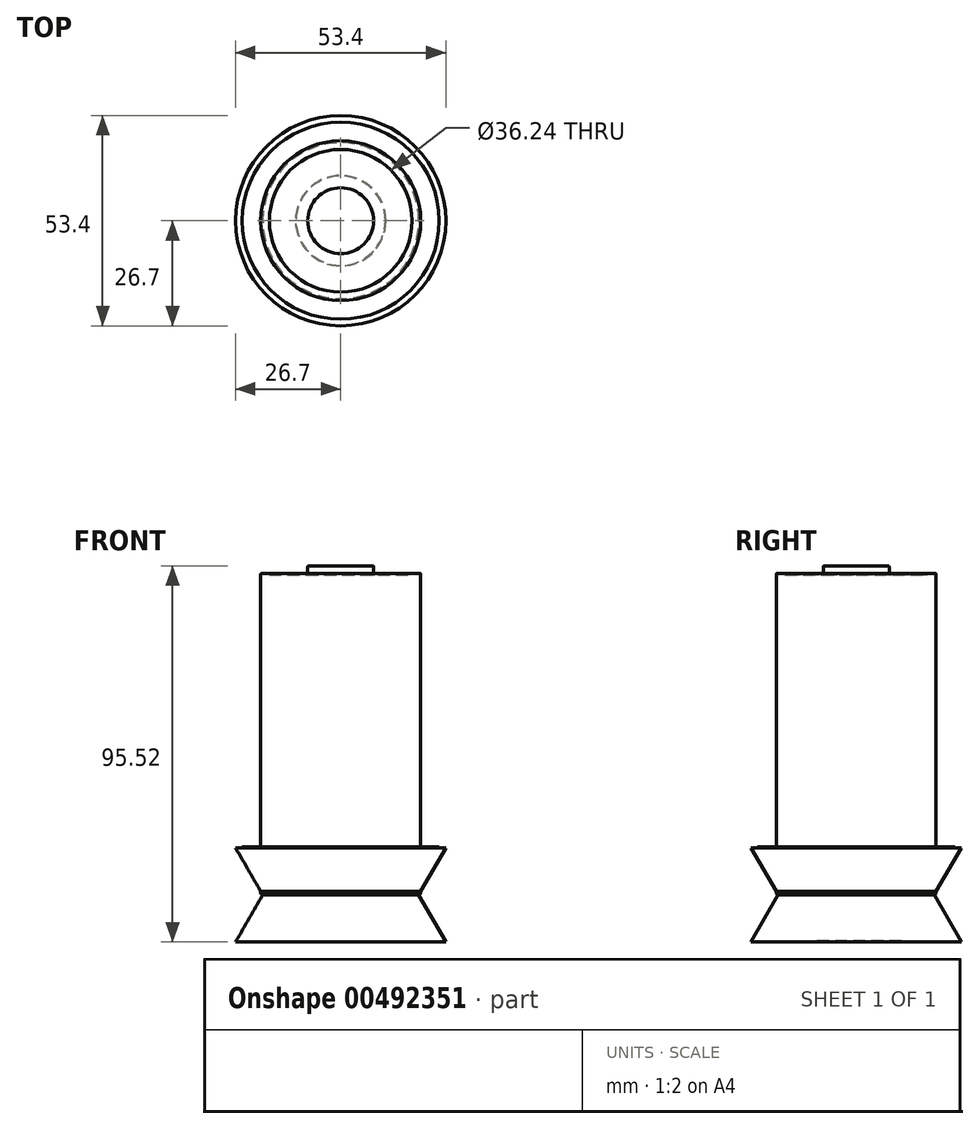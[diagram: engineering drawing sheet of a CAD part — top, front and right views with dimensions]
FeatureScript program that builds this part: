
annotation { "Feature Type Name" : "Feature", "Feature Type Description" : "" }
export const myFeature = defineFeature(function(context is Context, id is Id, definition is map)
    precondition{}
    {
        {
            var Q0;
            Q0=qCreatedBy(makeId("Right.planeOp"),FACE);
            var sketch = newSketch(context, id + "F0", { "sketchPlane" : qUnion([Q0])});
            skLineSegment(sketch, "E0", {"start": v(0, 0) * mm, "end": v(0, 48.96) * mm});
            skLineSegment(sketch, "E1", {"start": v(0, 0) * mm, "end": v(0, -32.32) * mm});
            skLineSegment(sketch, "E2", {"start": v(18.25, -32.32) * mm, "end": v(19.81, -32.32) * mm});
            skLineSegment(sketch, "E3", {"start": v(18.1, 48.96) * mm, "end": v(8.63, 48.96) * mm});
            skLineSegment(sketch, "E4", {"start": v(20.32, 48.96) * mm, "end": v(20.32, -31.81) * mm});
            skLineSegment(sketch, "E5", {"start": v(8.38, 49.2) * mm, "end": v(8.38, 51.01) * mm});
            skLineSegment(sketch, "E6", {"start": v(0, 51.26) * mm, "end": v(0, 48.96) * mm});
            skLineSegment(sketch, "E7", {"start": v(0, 51.26) * mm, "end": v(8.13, 51.26) * mm});
            skLineSegment(sketch, "E8.top", {"start": v(18.15, 49.32) * mm, "end": v(20.2, 49.32) * mm});
            skLineSegment(sketch, "E8.left", {"start": v(18.12, 48.99) * mm, "end": v(18.12, 49.3) * mm});
            skLineSegment(sketch, "E8.right", {"start": v(20.32, 48.45) * mm, "end": v(20.32, 49.19) * mm});
            skPoint(sketch, "E9.visualSharp", {"position": v(18.12, 49.32) * mm});
            skArc(sketch, "E9.filletArc", {"start": v(18.15, 49.32) * mm, "mid": v(18.13, 49.3) * mm, "end": v(18.12, 49.3) * mm});
            skPoint(sketch, "E10.visualSharp", {"position": v(20.32, 49.32) * mm});
            skArc(sketch, "E10.filletArc", {"start": v(20.32, 49.19) * mm, "mid": v(20.28, 49.28) * mm, "end": v(20.2, 49.32) * mm});
            skPoint(sketch, "E11.visualSharp", {"position": v(18.12, 48.96) * mm});
            skArc(sketch, "E11.filletArc", {"start": v(18.1, 48.96) * mm, "mid": v(18.11, 48.97) * mm, "end": v(18.12, 48.99) * mm});
            skPoint(sketch, "E12.visualSharp", {"position": v(8.38, 48.96) * mm});
            skArc(sketch, "E12.filletArc", {"start": v(8.38, 49.2) * mm, "mid": v(8.45, 49.03) * mm, "end": v(8.63, 48.96) * mm});
            skPoint(sketch, "E13.visualSharp", {"position": v(8.38, 51.26) * mm});
            skArc(sketch, "E13.filletArc", {"start": v(8.38, 51.01) * mm, "mid": v(8.3, 51.19) * mm, "end": v(8.13, 51.26) * mm});
            skPoint(sketch, "E14.visualSharp", {"position": v(20.32, -32.32) * mm});
            skArc(sketch, "E14.filletArc", {"start": v(19.81, -32.32) * mm, "mid": v(20.17, -32.17) * mm, "end": v(20.32, -31.81) * mm});
            skLineSegment(sketch, "E15", {"start": v(0, -32.1) * mm, "end": v(18.14, -32.1) * mm});
            skLineSegment(sketch, "E16", {"start": v(18.2, -32.16) * mm, "end": v(18.2, -32.26) * mm});
            skPoint(sketch, "E17.visualSharp", {"position": v(18.2, -32.32) * mm});
            skArc(sketch, "E17.filletArc", {"start": v(18.2, -32.26) * mm, "mid": v(18.2, -32.3) * mm, "end": v(18.25, -32.32) * mm});
            skPoint(sketch, "E18.visualSharp", {"position": v(18.2, -32.1) * mm});
            skArc(sketch, "E18.filletArc", {"start": v(18.2, -32.16) * mm, "mid": v(18.18, -32.12) * mm, "end": v(18.14, -32.1) * mm});
            skSolve(sketch);
        }
        {
            var Q0;
            Q0 = qSketchRegion(id + "F0", true);
            var Q1;
            Q1=sQuery(id+"F0.wireOp",EDGE,"E0");
            revolve(context, id + "F1", {"entities" : qUnion([Q0]), "axis" : qUnion([Q1]), "revolveType" : RevolveType.FULL});
        }
        {
            var Q0;
            Q0=makeQuery(id+"F1.opRevolve","SWEPT_FACE",FACE,{"disambiguationData":[OSD([sQuery(id+"F0.wireOp",EDGE,"E15")])]});
            var Q1;
            Q1=makeQuery(id+"F1.opRevolve","SWEPT_FACE",FACE,{"disambiguationData":[OSD([sQuery(id+"F0.wireOp",EDGE,"E2")])]});
            extrude(context, id + "F2", {"entities" : qUnion([Q0, Q1]), "operationType" : NewBodyOperationType.ADD, "endBound" : BoundingType.SYMMETRIC, "depth" : 23.88 * mm, "hasDraft" : true, "draftAngle" : 30 * degree});
        }
    });
